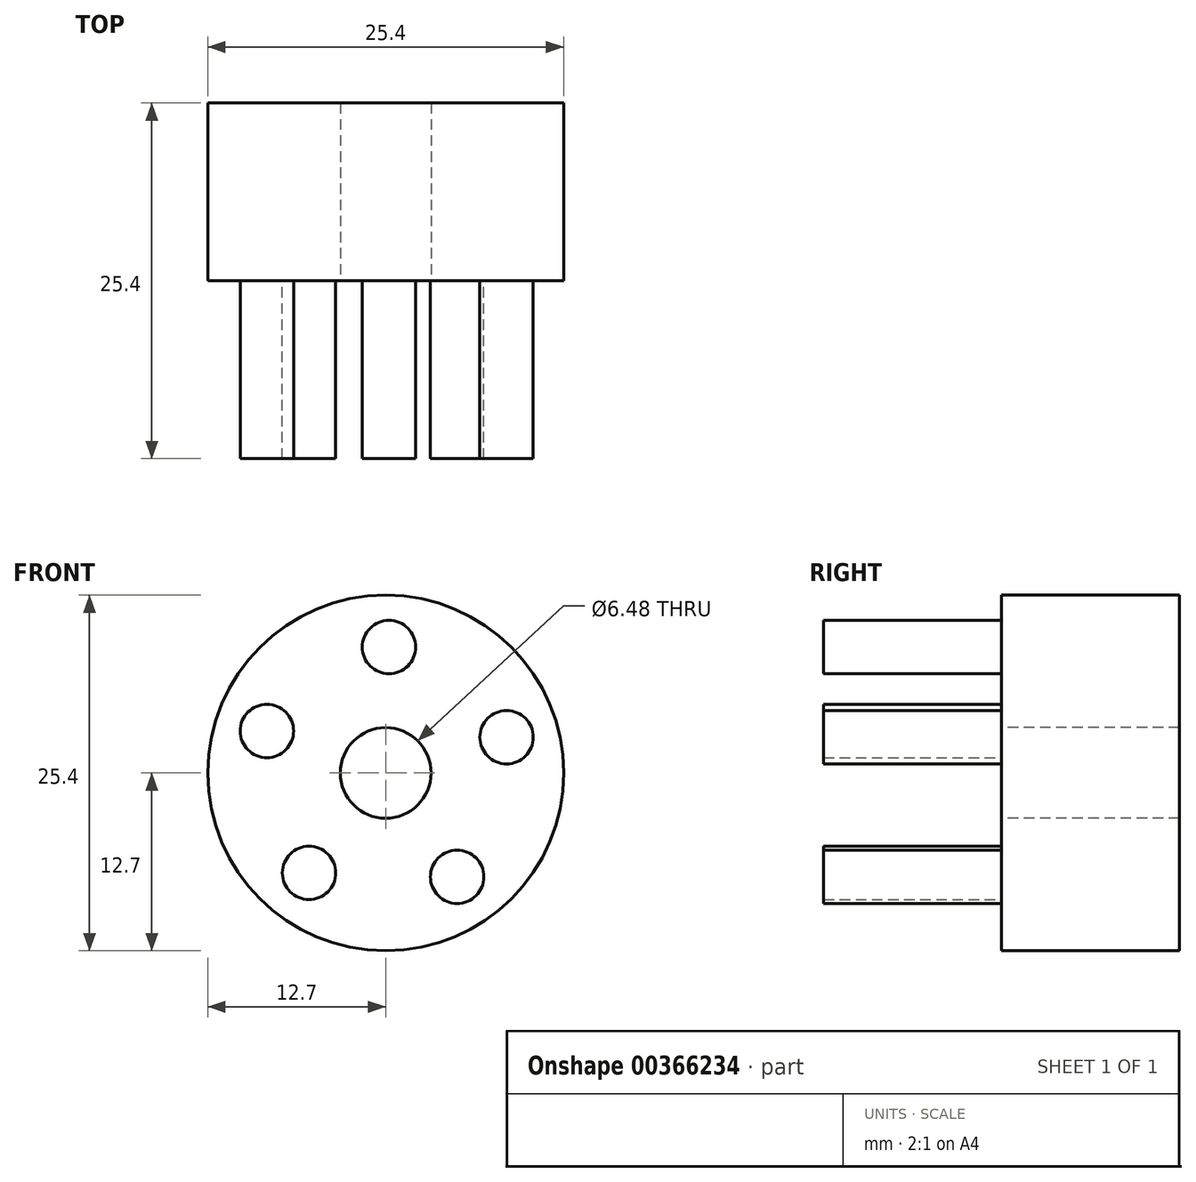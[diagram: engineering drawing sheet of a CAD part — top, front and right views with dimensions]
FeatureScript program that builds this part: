
annotation { "Feature Type Name" : "Feature", "Feature Type Description" : "" }
export const myFeature = defineFeature(function(context is Context, id is Id, definition is map)
    precondition{}
    {
        {
            var Q0;
            Q0=qCreatedBy(makeId("Front.planeOp"),FACE);
            var sketch = newSketch(context, id + "F0", { "sketchPlane" : qUnion([Q0])});
            skCircle(sketch, "E0", {"center": v(0, 0) * mm, "radius": 12.7 * mm});
            skSolve(sketch);
        }
        {
            var Q0;
            Q0=makeQuery(id+"F0.imprint","IMPRINT",FACE,{"disambiguationData":[TD([[makeQuery(id+"F0.imprint","IMPRINT",EDGE,{"derivedFrom":sQuery(id+"F0.wireOp",EDGE,"E0")}),1.0]])]});
            extrude(context, id + "F1", {"entities" : qUnion([Q0]), "depth" : 12.7 * mm});
        }
        {
            var Q0;
            Q0=makeQuery(id+"F1.opExtrude","CAP_FACE",FACE,{"disambiguationData":[OSD([sQuery(id+"F0.wireOp",EDGE,"E0")])],"isStart":false});
            var sketch = newSketch(context, id + "F2", { "sketchPlane" : qUnion([Q0])});
            skCircle(sketch, "E1", {"center": v(0, 0) * mm, "radius": 3.24 * mm});
            skSolve(sketch);
        }
        {
            var Q0;
            Q0 = qSketchRegion(id + "F2", true);
            extrude(context, id + "F3", {"entities" : qUnion([Q0]), "operationType" : NewBodyOperationType.REMOVE, "oppositeDirection" : true, "depth" : 12.7 * mm});
        }
        {
            var Q0;
            Q0=makeQuery(id+"F1.opExtrude","CAP_FACE",FACE,{"disambiguationData":[OSD([sQuery(id+"F0.wireOp",EDGE,"E0")])],"isStart":false});
            var sketch = newSketch(context, id + "F4", { "sketchPlane" : qUnion([Q0])});
            skCircle(sketch, "E2", {"center": v(-8.48, 3) * mm, "radius": 1.9 * mm});
            skCircle(sketch, "E3.1.0", {"center": v(-5.48, -7.14) * mm, "radius": 1.9 * mm});
            skCircle(sketch, "E3.2.0", {"center": v(5.1, -7.41) * mm, "radius": 1.9 * mm});
            skCircle(sketch, "E3.3.0", {"center": v(8.63, 2.56) * mm, "radius": 1.9 * mm});
            skCircle(sketch, "E3.4.0", {"center": v(0.23, 9) * mm, "radius": 1.9 * mm});
            skPoint(sketch, "E3.center", {"position": v(0, 0) * mm});
            skSolve(sketch);
        }
        {
            var Q0;
            Q0 = qSketchRegion(id + "F4", true);
            extrude(context, id + "F5", {"entities" : qUnion([Q0]), "operationType" : NewBodyOperationType.ADD, "depth" : 12.7 * mm});
        }
    });
